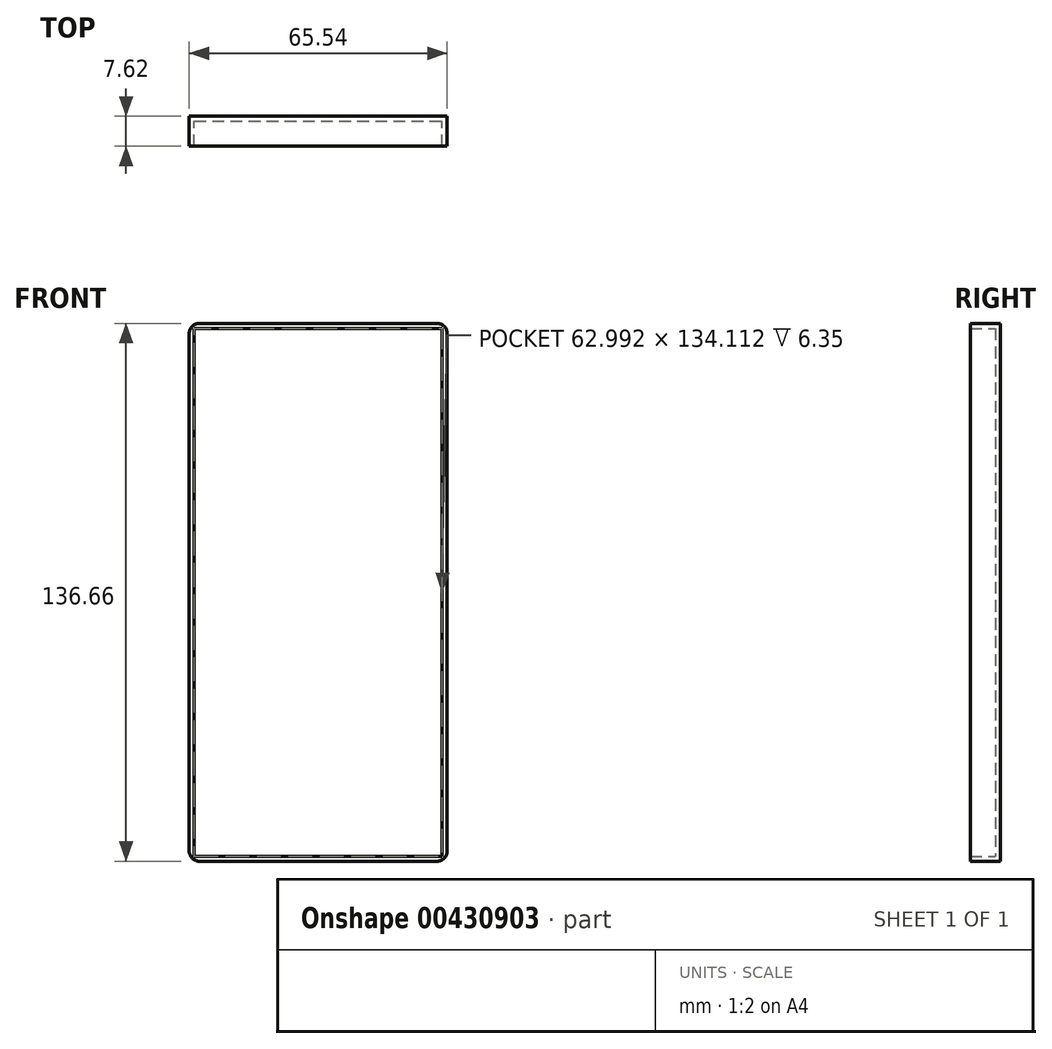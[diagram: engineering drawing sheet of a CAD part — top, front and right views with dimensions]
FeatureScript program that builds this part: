
annotation { "Feature Type Name" : "Feature", "Feature Type Description" : "" }
export const myFeature = defineFeature(function(context is Context, id is Id, definition is map)
    precondition{}
    {
        {
            var Q0;
            Q0=qCreatedBy(makeId("Front.planeOp"),FACE);
            var sketch = newSketch(context, id + "F0", { "sketchPlane" : qUnion([Q0])});
            skLineSegment(sketch, "E0.bottom", {"start": v(-32.77, 68.33) * mm, "end": v(32.77, 68.33) * mm});
            skLineSegment(sketch, "E0.top", {"start": v(-32.77, -68.33) * mm, "end": v(32.77, -68.33) * mm});
            skLineSegment(sketch, "E0.left", {"start": v(-32.77, 68.33) * mm, "end": v(-32.77, -68.33) * mm});
            skLineSegment(sketch, "E0.right", {"start": v(32.77, 68.33) * mm, "end": v(32.77, -68.33) * mm});
            skPoint(sketch, "E0.middle", {"position": v(0, 0) * mm});
            skSolve(sketch);
        }
        {
            var Q0;
            Q0=makeQuery(id+"F0.imprint","IMPRINT",FACE,{"disambiguationData":[TD([[makeQuery(id+"F0.imprint","IMPRINT",EDGE,{"derivedFrom":sQuery(id+"F0.wireOp",EDGE,"E0.bottom")}),-1.0]])]});
            extrude(context, id + "F1", {"entities" : qUnion([Q0]), "depth" : 7.62 * mm});
        }
        {
            var Q0;
            Q0=makeQuery(id+"F1.opExtrude","CAP_FACE",FACE,{"disambiguationData":[OSD([sQuery(id+"F0.wireOp",EDGE,"E0.bottom"),sQuery(id+"F0.wireOp",EDGE,"E0.top"),sQuery(id+"F0.wireOp",EDGE,"E0.left"),sQuery(id+"F0.wireOp",EDGE,"E0.right")])],"isStart":false});
            shell(context, id + "F2", {"entities" : qUnion([Q0]), "thickness" : 1.27 * mm});
        }
        {
            var Q0;
            Q0=makeQuery(id+"F1.opExtrude","SWEPT_EDGE",EDGE,{"disambiguationData":[OSD([sQuery(id+"F0.wireOp",EDGE,"E0.top"),sQuery(id+"F0.wireOp",EDGE,"E0.left")])]});
            var Q1;
            Q1=makeQuery(id+"F1.opExtrude","SWEPT_EDGE",EDGE,{"disambiguationData":[OSD([sQuery(id+"F0.wireOp",EDGE,"E0.top"),sQuery(id+"F0.wireOp",EDGE,"E0.right")])]});
            var Q2;
            Q2=makeQuery(id+"F1.opExtrude","SWEPT_EDGE",EDGE,{"disambiguationData":[OSD([sQuery(id+"F0.wireOp",EDGE,"E0.bottom"),sQuery(id+"F0.wireOp",EDGE,"E0.right")])]});
            var Q3;
            Q3=makeQuery(id+"F1.opExtrude","SWEPT_EDGE",EDGE,{"disambiguationData":[OSD([sQuery(id+"F0.wireOp",EDGE,"E0.bottom"),sQuery(id+"F0.wireOp",EDGE,"E0.left")])]});
            fillet(context, id + "F3", {"entities" : qUnion([Q0, Q1, Q2, Q3]), "radius" : 2.54 * mm, "tangentPropagation" : true, "allowEdgeOverflow" : false});
        }
    });
